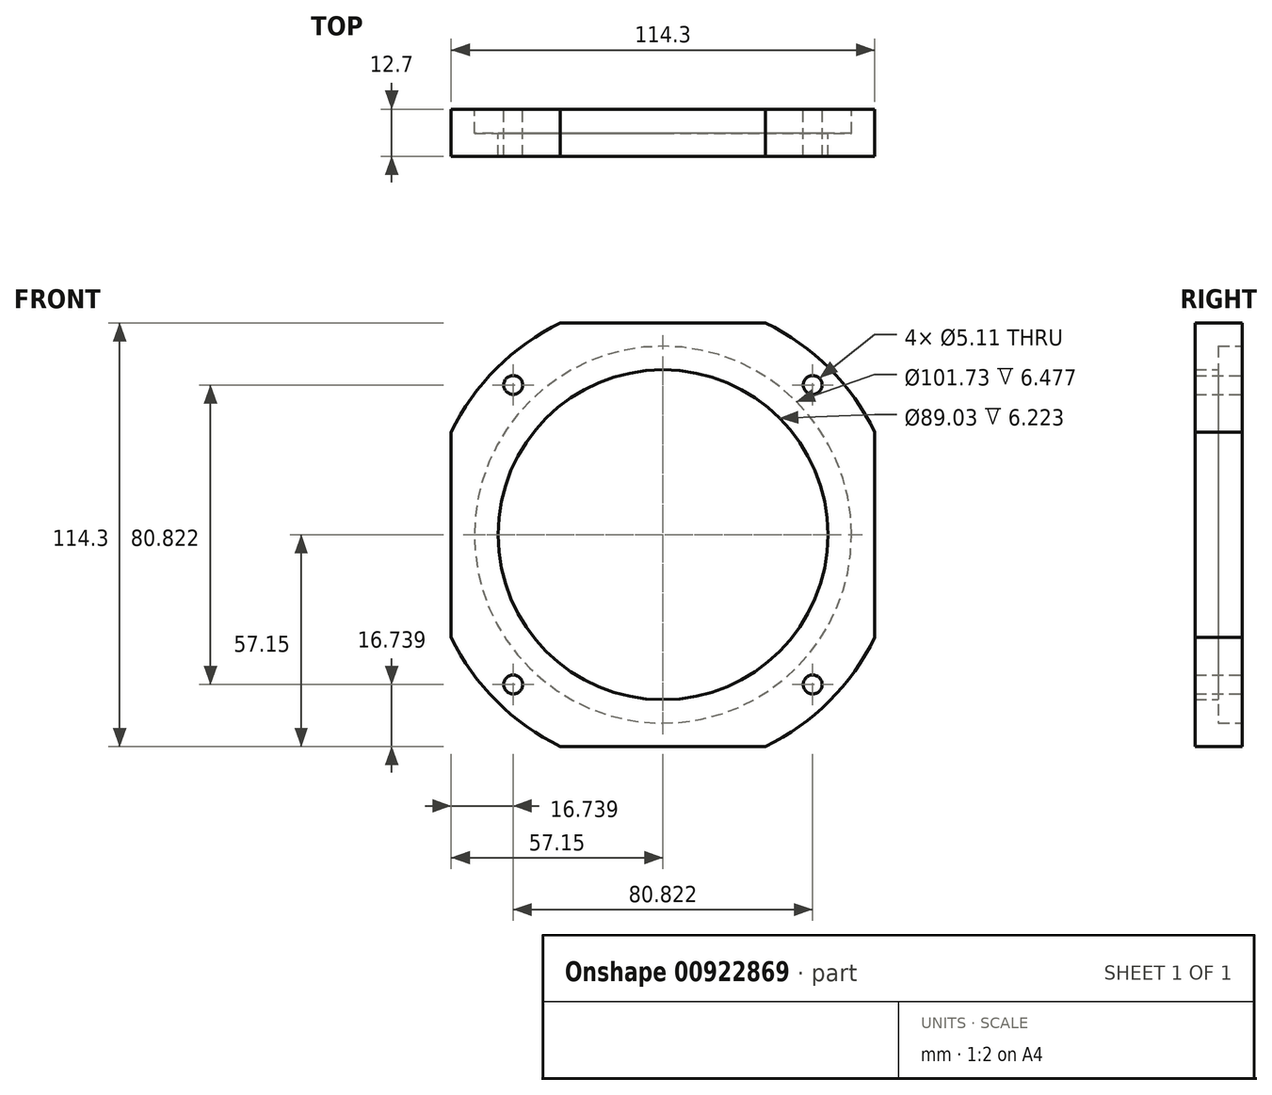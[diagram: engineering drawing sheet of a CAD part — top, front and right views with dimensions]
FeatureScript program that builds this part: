
annotation { "Feature Type Name" : "Feature", "Feature Type Description" : "" }
export const myFeature = defineFeature(function(context is Context, id is Id, definition is map)
    precondition{}
    {
        {
            var Q0;
            Q0=qCreatedBy(makeId("Front.planeOp"),FACE);
            var sketch = newSketch(context, id + "F0", { "sketchPlane" : qUnion([Q0])});
            skLineSegment(sketch, "E0.bottom", {"start": v(57.15, 57.15) * mm, "end": v(-57.15, 57.15) * mm});
            skLineSegment(sketch, "E0.top", {"start": v(57.15, -57.15) * mm, "end": v(-57.15, -57.15) * mm});
            skLineSegment(sketch, "E0.left", {"start": v(57.15, 57.15) * mm, "end": v(57.15, -57.15) * mm});
            skLineSegment(sketch, "E0.right", {"start": v(-57.15, 57.15) * mm, "end": v(-57.15, -57.15) * mm});
            skPoint(sketch, "E0.middle", {"position": v(0, 0) * mm});
            skSolve(sketch);
        }
        {
            var Q0;
            Q0 = qSketchRegion(id + "F0", true);
            extrude(context, id + "F1", {"entities" : qUnion([Q0]), "oppositeDirection" : true, "depth" : 12.7 * mm, "offsetDistance" : 25.4 * mm});
        }
        {
            var Q0;
            Q0=makeQuery(id+"F1.opExtrude","CAP_FACE",FACE,{"disambiguationData":[OSD([sQuery(id+"F0.wireOp",EDGE,"E0.bottom"),sQuery(id+"F0.wireOp",EDGE,"E0.top"),sQuery(id+"F0.wireOp",EDGE,"E0.left"),sQuery(id+"F0.wireOp",EDGE,"E0.right")])],"isStart":false});
            var sketch = newSketch(context, id + "F2", { "sketchPlane" : qUnion([Q0])});
            skCircle(sketch, "E1", {"center": v(0, 0) * mm, "radius": 50.86 * mm});
            skSolve(sketch);
        }
        {
            var Q0;
            Q0 = qSketchRegion(id + "F2", true);
            extrude(context, id + "F3", {"entities" : qUnion([Q0]), "operationType" : NewBodyOperationType.REMOVE, "oppositeDirection" : true, "depth" : 6.48 * mm, "offsetDistance" : 25.4 * mm});
        }
        {
            var Q0;
            Q0=makeQuery(id+"F3.boolean.opBoolean","COPY",FACE,{"derivedFrom":makeQuery(id+"F3.opExtrude","CAP_FACE",FACE,{"disambiguationData":[OSD([sQuery(id+"F2.wireOp",EDGE,"E1")])],"isStart":false})});
            var sketch = newSketch(context, id + "F4", { "sketchPlane" : qUnion([Q0])});
            skCircle(sketch, "E2", {"center": v(0, 0) * mm, "radius": 44.51 * mm});
            skSolve(sketch);
        }
        {
            var Q0;
            Q0 = qSketchRegion(id + "F4", true);
            extrude(context, id + "F5", {"entities" : qUnion([Q0]), "operationType" : NewBodyOperationType.REMOVE, "endBound" : BoundingType.THROUGH_ALL, "oppositeDirection" : true, "depth" : 25.4 * mm, "offsetDistance" : 25.4 * mm});
        }
        {
            var Q0;
            Q0=makeQuery(id+"F1.opExtrude","SWEPT_EDGE",EDGE,{"disambiguationData":[OSD([sQuery(id+"F0.wireOp",EDGE,"E0.bottom"),sQuery(id+"F0.wireOp",EDGE,"E0.left")])]});
            var Q1;
            Q1=makeQuery(id+"F1.opExtrude","SWEPT_EDGE",EDGE,{"disambiguationData":[OSD([sQuery(id+"F0.wireOp",EDGE,"E0.bottom"),sQuery(id+"F0.wireOp",EDGE,"E0.right")])]});
            var Q2;
            Q2=makeQuery(id+"F1.opExtrude","SWEPT_EDGE",EDGE,{"disambiguationData":[OSD([sQuery(id+"F0.wireOp",EDGE,"E0.top"),sQuery(id+"F0.wireOp",EDGE,"E0.left")])]});
            var Q3;
            Q3=makeQuery(id+"F1.opExtrude","SWEPT_EDGE",EDGE,{"disambiguationData":[OSD([sQuery(id+"F0.wireOp",EDGE,"E0.top"),sQuery(id+"F0.wireOp",EDGE,"E0.right")])]});
            fillet(context, id + "F6", {"entities" : qUnion([Q0, Q1, Q2, Q3]), "radius" : 9.52 * mm, "tangentPropagation" : true, "allowEdgeOverflow" : false});
        }
        {
            var Q0;
            Q0=makeQuery(id+"F1.opExtrude","CAP_FACE",FACE,{"disambiguationData":[OSD([sQuery(id+"F0.wireOp",EDGE,"E0.bottom"),sQuery(id+"F0.wireOp",EDGE,"E0.top"),sQuery(id+"F0.wireOp",EDGE,"E0.left"),sQuery(id+"F0.wireOp",EDGE,"E0.right")])],"isStart":false});
            var sketch = newSketch(context, id + "F7", { "sketchPlane" : qUnion([Q0])});
            skPoint(sketch, "E3", {"position": v(-47.63, 47.62) * mm});
            skPoint(sketch, "E4", {"position": v(47.62, 47.63) * mm});
            skPoint(sketch, "E5", {"position": v(47.63, -47.62) * mm});
            skPoint(sketch, "E6", {"position": v(-47.63, -47.63) * mm});
            skSolve(sketch);
        }
        {
            var Q0;
            Q0=sQuery(id+"F7.wireOp",VERTEX,"E3");
            var Q1;
            Q1=sQuery(id+"F7.wireOp",VERTEX,"E5");
            var Q2;
            Q2=sQuery(id+"F7.wireOp",VERTEX,"E4");
            var Q3;
            Q3=sQuery(id+"F7.wireOp",VERTEX,"E6");
            var Q4;
            Q4=makeQuery(id+"F1.opExtrude","SWEPT_BODY",BODY,{"disambiguationData":[OSD([sQuery(id+"F0.wireOp",EDGE,"E0.bottom"),sQuery(id+"F0.wireOp",EDGE,"E0.top"),sQuery(id+"F0.wireOp",EDGE,"E0.left"),sQuery(id+"F0.wireOp",EDGE,"E0.right")])]});
            hole(context, id + "F8", {"style" : HoleStyle.SIMPLE, "endStyle" : HoleEndStyle.THROUGH, "standardTappedOrClearance" : lookupTablePath({ "standard" : "ANSI", "engagement" : "75%", "pitch" : "20 tpi", "size" : "1/4", "type" : "Tapped" }), "standardBlindInLast" : lookupTablePath({ "standard" : "ANSI", "engagement" : "75%", "pitch" : "20 tpi", "size" : "1/4", "type" : "Tapped" }), "holeDiameter" : 5.1 * mm, "majorDiameter" : 6.35 * mm, "showTappedDepth" : true, "isTappedThrough" : true, "tappedDepth" : 12.7 * mm, "tapClearance" : 3, "locations" : qUnion([Q0, Q1, Q2, Q3]), "scope" : qUnion([Q4])});
        }
        {
            var Q0;
            Q0=qCreatedBy(makeId("Front.planeOp"),FACE);
            var sketch = newSketch(context, id + "F9", { "sketchPlane" : qUnion([Q0])});
            skCircle(sketch, "E7", {"center": v(0, 0) * mm, "radius": 63.5 * mm});
            skCircle(sketch, "E8", {"center": v(0, 0) * mm, "radius": 110.54 * mm});
            skSolve(sketch);
        }
        {
            var Q0;
            Q0 = qSketchRegion(id + "F9", true);
            extrude(context, id + "F10", {"entities" : qUnion([Q0]), "operationType" : NewBodyOperationType.REMOVE, "oppositeDirection" : true, "depth" : 25.4 * mm, "offsetDistance" : 25.4 * mm});
        }
        {
            var Q0;
            Q0=makeQuery(id+"F1.opExtrude","CAP_FACE",FACE,{"disambiguationData":[OSD([sQuery(id+"F0.wireOp",EDGE,"E0.bottom"),sQuery(id+"F0.wireOp",EDGE,"E0.top"),sQuery(id+"F0.wireOp",EDGE,"E0.left"),sQuery(id+"F0.wireOp",EDGE,"E0.right")])],"isStart":false});
            var sketch = newSketch(context, id + "F11", { "sketchPlane" : qUnion([Q0])});
            skPoint(sketch, "E9", {"position": v(40.41, 40.41) * mm});
            skLineSegment(sketch, "E10.bottom", {"start": v(40.41, 40.41) * mm, "end": v(-40.41, 40.41) * mm});
            skLineSegment(sketch, "E10.top", {"start": v(40.41, -40.41) * mm, "end": v(-40.41, -40.41) * mm});
            skLineSegment(sketch, "E10.left", {"start": v(40.41, 40.41) * mm, "end": v(40.41, -40.41) * mm});
            skLineSegment(sketch, "E10.right", {"start": v(-40.41, 40.41) * mm, "end": v(-40.41, -40.41) * mm});
            skPoint(sketch, "E10.middle", {"position": v(0, 0) * mm});
            skSolve(sketch);
        }
        {
            var Q0;
            Q0=sQuery(id+"F11.wireOp",VERTEX,"E9");
            var Q1;
            Q1=sQuery(id+"F11.wireOp",VERTEX,"E10.bottom.end");
            var Q2;
            Q2=sQuery(id+"F11.wireOp",VERTEX,"E10.top.end");
            var Q3;
            Q3=sQuery(id+"F11.wireOp",VERTEX,"E10.top.start");
            var Q4;
            Q4=makeQuery(id+"F1.opExtrude","SWEPT_BODY",BODY,{"disambiguationData":[OSD([sQuery(id+"F0.wireOp",EDGE,"E0.bottom"),sQuery(id+"F0.wireOp",EDGE,"E0.top"),sQuery(id+"F0.wireOp",EDGE,"E0.left"),sQuery(id+"F0.wireOp",EDGE,"E0.right")])]});
            hole(context, id + "F12", {"style" : HoleStyle.SIMPLE, "endStyle" : HoleEndStyle.THROUGH, "standardTappedOrClearance" : lookupTablePath({ "standard" : "ANSI", "engagement" : "75%", "pitch" : "20 tpi", "size" : "1/4", "type" : "Tapped" }), "standardBlindInLast" : lookupTablePath({ "standard" : "ANSI", "engagement" : "75%", "pitch" : "20 tpi", "size" : "1/4", "type" : "Tapped" }), "holeDiameter" : 5.1 * mm, "majorDiameter" : 6.35 * mm, "showTappedDepth" : true, "isTappedThrough" : true, "tappedDepth" : 12.7 * mm, "tapClearance" : 3, "locations" : qUnion([Q0, Q1, Q2, Q3]), "scope" : qUnion([Q4])});
        }
    });
